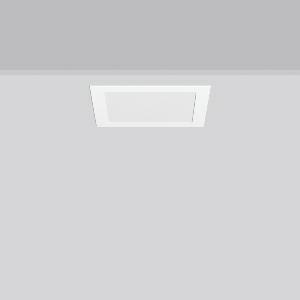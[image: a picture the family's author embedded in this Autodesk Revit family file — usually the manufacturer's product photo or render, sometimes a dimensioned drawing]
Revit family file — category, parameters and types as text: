
# Revit family: toledo_flat_square_e_672243_002_1_eda2
name_source: partatom
category: Lighting Fixtures
units: mm (PartAtom-declared; Revit-internal decimal feet)

## family parameters
Cut with Voids When Loaded = No
Host = Face
Light Source = No
Part Type = Normal
Room Calculation Point = No
Round Connector Dimension = Use Diameter
Shared = No

## types (1)
- TOLEDO FLAT square E (1 x LED Modul 840, 1650 lm, 4000)
    Apparent Load = 18 VA
    CIE Flux Codes = 49 80 96 100 100
    Color Rendering = 80
    Color Temperature = 4000
    Default Elevation = 1800 mm
    Description = Series: TOLEDO FLAT square
Square recessed downlight. For escape route illumination. Housing: die-cast aluminium, powder-coated. Lightguide and diffuser made of non-yellowing plastic (PMMA). Diffuser opal matt plastic. Ceiling installation with spring system. Including separate LED converter with connecting cable 250 mm. Suitable for connection to central battery systems. External driver with simple plug-in locking system. 
Colour: white
Length: 225 mm
Width: 225 mm
Height: 3 mm
Cut-out length: 208 mm
Cut-out width: 208 mm
Recess height: 35 mm
Luminaire: recess height: 31-51 mm
Weight: 0.653 kg
Operating mode: maintained power mode
Lamp: LED
Socket: without socket
Colour temperature: 4000K
Colour rendering index (CRI): 80
System power: 18 W
Rated luminous flux: 1650 lm
Luminous flux, emergency: 1650 lm
System power, emergency: 18 W
Control gear: Regulated power supply
Protection class: II
Type of protection: IP 54
    Height = 0 mm  [stored 0 ft]
    Lamp = 1 x LED Modul 840
    Lamp Light Flux = 1650 lm
    Lamp count = 1
    Length = 225 mm
    Lifetime = 50000 h
    Luminous efficacy = 92 lm/W
    Manufacturer = RZB
    ModVariant = No
    Model = 672243.002.1
    Mounting Place = Ceiling
    Mounting Type = Recessed
    Number of Poles = 1
    OnlyDefault = Yes
    Power Factor = 1
    Product Name = TOLEDO FLAT square E
    Product group = Recessed downlights
    ProductGroupID = 402
    Protection Class = Protection class II
    Protection Degree = IP 40
    RLX_Detail_Level = 1
    RLX_Emergency_Light_Flux = 1650 lm
    RLX_Emergency_Type = 3
    RLX_Emergency_Type_DB = Yes
    RlxData = <blob elided: 10953 chars, md5=8bc01f11>
    Socket = socket
    Standby Power = 0 W
    System Light Flux = 1650 lm
    System Power = 18 W
    Type Comments = Product without accessories
    Type Image = 901487.002.jpg
    URL = http://relux.com
    VarID = ---
    Voltage = 230 V
    Voltage Range = 220-240 V
    Weight = 0.00 kg
    Width = 225 mm

note: [stored X ft] marks values corroborated as IEEE doubles in the binary element streams (Revit-internal decimal feet)

## geometry (parser evidence)
native form markers: Sweep x8
no freeform markers — native parametric forms only
